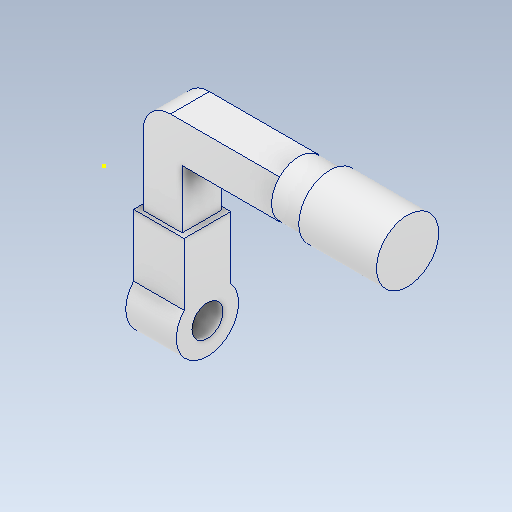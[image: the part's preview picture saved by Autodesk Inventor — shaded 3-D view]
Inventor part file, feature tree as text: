
AUTODESK INVENTOR PART (.ipt)
format: ipt  version: 2021 (Build 250183000, 183)  size: 146,432 bytes
history: native  units: mm
features: sketch x7, other x3, plane x1
ambient origin geometry x8: Origin, YZ Plane, XZ Plane, XY Plane, X Axis, Y Axis, Z Axis, Center Point
bodies: Solid1 (feature_tree)
feature tree (11):
  other  "Waist Adjustment Part.ipt"
  other  "Solid1::Waist Adjustment Part.ipt"
  other  "TaggingFeature1"
  sketch  "Sketch1"  dims[d0=10.0mm]
  sketch  "Sketch2"
  sketch  "Sketch3"
  sketch  "Sketch4"
  sketch  "Sketch5"
  sketch  "Sketch6"
  sketch  "3D Sketch1"
  plane  "Work Plane1"
